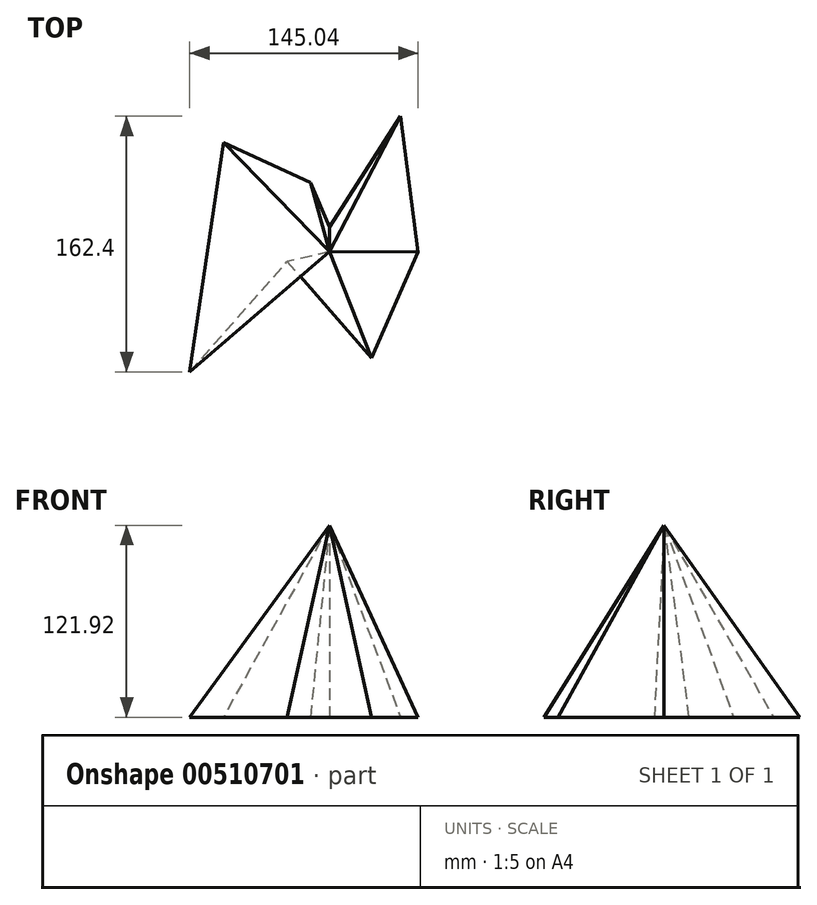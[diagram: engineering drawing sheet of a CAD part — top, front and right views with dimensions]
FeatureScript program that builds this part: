
annotation { "Feature Type Name" : "Feature", "Feature Type Description" : "" }
export const myFeature = defineFeature(function(context is Context, id is Id, definition is map)
    precondition{}
    {
        {
            var Q0;
            Q0=qCreatedBy(makeId("Top.planeOp"),FACE);
            var sketch = newSketch(context, id + "F0", { "sketchPlane" : qUnion([Q0])});
            skLineSegment(sketch, "E0", {"start": v(-67.42, 69.5) * mm, "end": v(-88.78, -76.3) * mm});
            skLineSegment(sketch, "E1", {"start": v(-88.78, -76.3) * mm, "end": v(-26.74, -6.11) * mm});
            skLineSegment(sketch, "E2", {"start": v(-27.08, -6.11) * mm, "end": v(26.83, -67.48) * mm});
            skLineSegment(sketch, "E3", {"start": v(26.83, -67.48) * mm, "end": v(56.33, 0) * mm});
            skLineSegment(sketch, "E4", {"start": v(56.33, -0.69) * mm, "end": v(45.14, 86.1) * mm});
            skLineSegment(sketch, "E5", {"start": v(45.14, 86.1) * mm, "end": v(0, 15.59) * mm});
            skLineSegment(sketch, "E6", {"start": v(0, 15.59) * mm, "end": v(-12.16, 44.07) * mm});
            skLineSegment(sketch, "E7", {"start": v(-12.16, 44.07) * mm, "end": v(-67.42, 69.5) * mm});
            skSolve(sketch);
        }
        {
            var Q0;
            Q0=qCreatedBy(makeId("Top.planeOp"),FACE);
            cPlane(context, id + "F1", {"entities" : qUnion([Q0]), "cplaneType" : CPlaneType.OFFSET, "offset" : 121.92 * mm, "width" : 152.4 * mm, "height" : 152.4 * mm});
        }
        {
            var Q0;
            Q0=qCreatedBy(id+"F1.planeOp",FACE);
            var sketch = newSketch(context, id + "F2", { "sketchPlane" : qUnion([Q0])});
            skPoint(sketch, "E8", {"position": v(0, 0) * mm});
            skSolve(sketch);
        }
        {
            var Q0;
            Q0=sQuery(id+"F2.wireOp",VERTEX,"E8");
            var Q1;
            {var subQ7=sQuery(id+"F0.wireOp",EDGE,"E0");Q1=makeQuery(id+"F0.imprint","IMPRINT",FACE,{"disambiguationData":[TD([[makeQuery(id+"F0.imprint","IMPRINT",EDGE,{"derivedFrom":subQ7}),1.0]])]});}
            loft(context, id + "F3", {"sheetProfilesArray" : [{ "sheetProfileEntities" : qUnion([Q0]) }, { "sheetProfileEntities" : qUnion([Q1]) }]});
        }
    });
